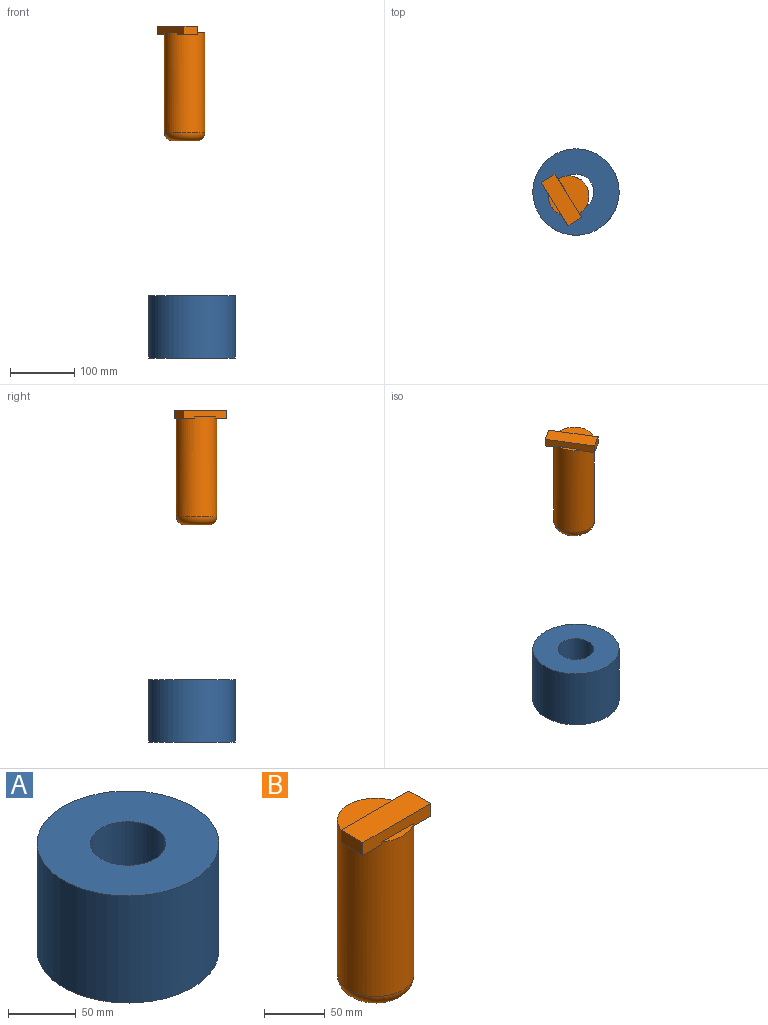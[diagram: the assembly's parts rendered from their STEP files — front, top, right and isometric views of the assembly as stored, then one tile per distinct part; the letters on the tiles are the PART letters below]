
ASSEMBLY  parts=2 mates=1
PART A: 4 faces, bbox 134.3x134.3x96.7 mm
  f0: cylinder r=27.82mm len=96.73mm, axis (0,0,-1), area 16908.1mm2, adj f2,f3
  f1: cylinder r=67.17mm len=134.33mm, axis (0,0,-1), area 40823.2mm2, adj f2,f3
  f2: plane 134.33x134.33mm, normal (0,0,1), area 11741.5mm2, adj f0,f1
  f3: plane 134.33x134.33mm, normal (0,0,-1), area 11741.5mm2, adj f0,f1
PART B: 12 faces, bbox 78.9x68.3x178.6 mm
  f0: plane 63.06x31.53mm, normal (0,0,1), area 1561.8mm2, adj f1,f7
  f1: cylinder r=31.53mm len=155.74mm, axis (0,0,-1), area 30710.8mm2, adj f0,f2,f4,f5,f6,f7,f10
  f2: plane 37.37x6.13mm, normal (0,0,1), area 156mm2, adj f1,f6
  f3: plane 37.81x37.81mm, normal (0,0,-1), area 1122.9mm2, adj f4
  f4: torus R=18.91mm, axis (0,0,1), area 3357.5mm2, adj f1,f3
  f5: plane 25.4x21.62mm, normal (0,0,-1), area 320.8mm2, adj f1,f6,f7,f9
  f6: plane 78.94x12.68mm, normal (0,-1,0), area 909mm2, adj f1,f2,f5,f8,f9,f10,f11
  f7: plane 78.94x12.68mm, normal (0,1,0), area 845.9mm2, adj f0,f1,f5,f8,f9,f10,f11
  f8: plane 78.94x25.4mm, normal (0,0,1), area 2005mm2, adj f6,f7,f9,f11
  f9: plane 25.4x12.68mm, normal (-1,0,0), area 322mm2, adj f5,f6,f7,f8
  f10: plane 25.4x19.95mm, normal (0,0,-1), area 278.4mm2, adj f1,f6,f7,f11
  f11: plane 25.4x12.68mm, normal (1,0,0), area 322mm2, adj f6,f7,f8,f10
PLACE A rot(axis=(0,0,-1),58.2deg) t=(-58.19,50.04,-19.45)mm fixed
PLACE B rot(axis=(0,0,-1),58.2deg) t=(-69.56,42.98,318.74)mm
MATE slider B.f0 <-> A.f0  axis (0,0,1) through (-58.19,50.04,487.11)mm
